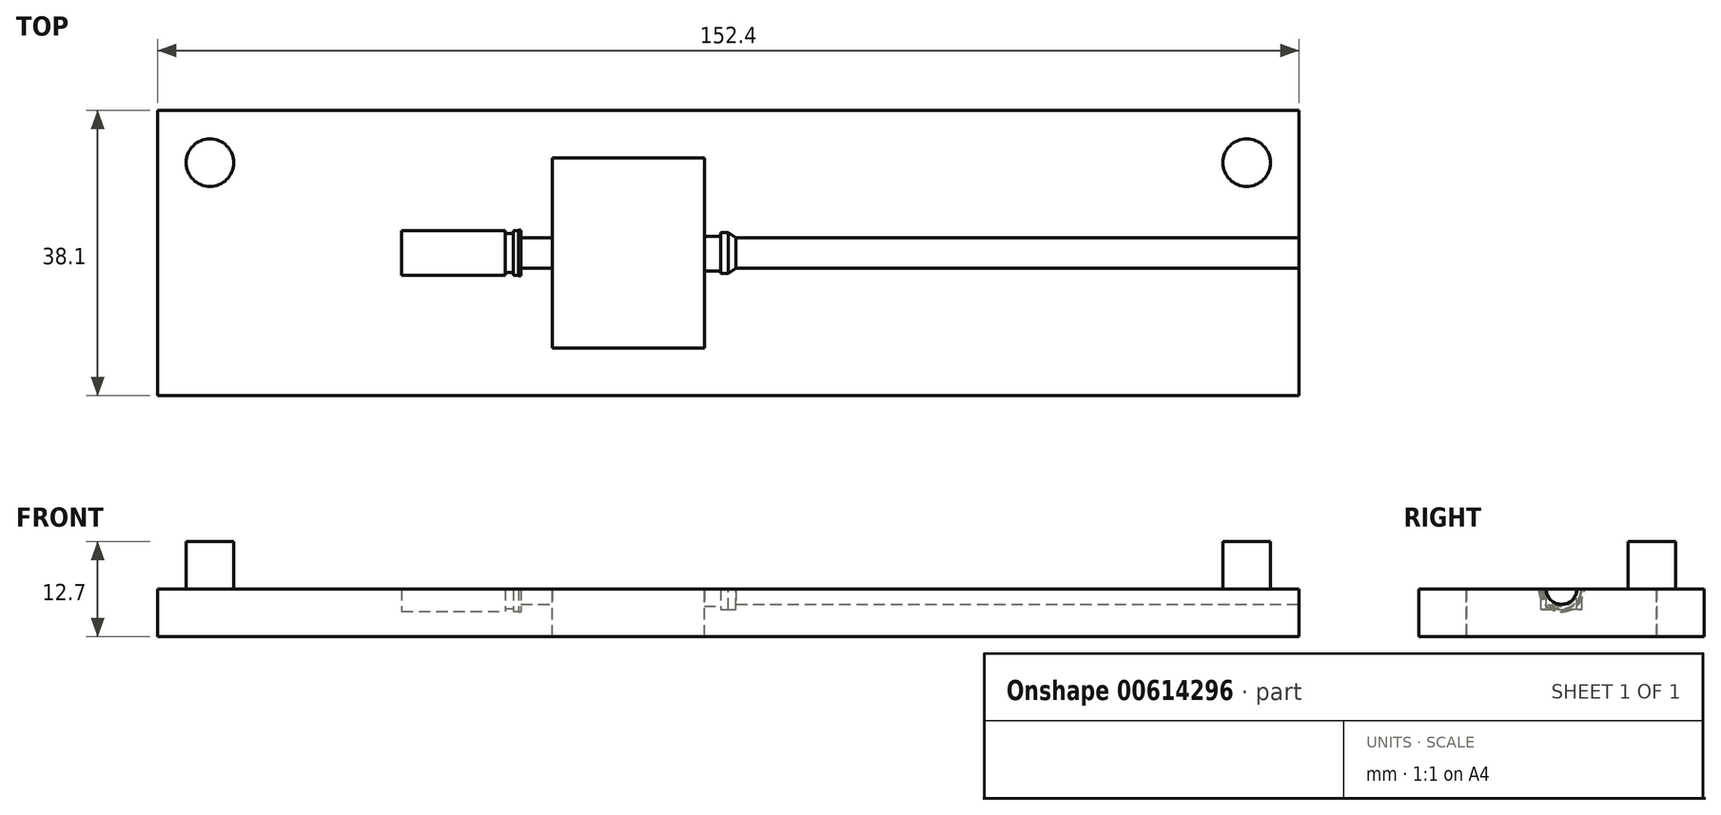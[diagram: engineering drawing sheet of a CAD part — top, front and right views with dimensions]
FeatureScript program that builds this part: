
annotation { "Feature Type Name" : "Feature", "Feature Type Description" : "" }
export const myFeature = defineFeature(function(context is Context, id is Id, definition is map)
    precondition{}
    {
        {
            var Q0;
            Q0=qCreatedBy(makeId("Top.planeOp"),FACE);
            var sketch = newSketch(context, id + "F0", { "sketchPlane" : qUnion([Q0])});
            skLineSegment(sketch, "E0.bottom", {"start": v(-76.2, 19.05) * mm, "end": v(76.2, 19.05) * mm});
            skLineSegment(sketch, "E0.top", {"start": v(-76.2, -19.05) * mm, "end": v(76.2, -19.05) * mm});
            skLineSegment(sketch, "E0.left", {"start": v(-76.2, 19.05) * mm, "end": v(-76.2, -19.05) * mm});
            skLineSegment(sketch, "E0.right", {"start": v(76.2, 19.05) * mm, "end": v(76.2, -19.05) * mm});
            skPoint(sketch, "E0.middle", {"position": v(0, 0) * mm});
            skSolve(sketch);
        }
        {
            var Q0;
            Q0=makeQuery(id+"F0.imprint","IMPRINT",FACE,{"disambiguationData":[TD([[makeQuery(id+"F0.imprint","IMPRINT",EDGE,{"derivedFrom":sQuery(id+"F0.wireOp",EDGE,"E0.bottom")}),-1.0]])]});
            extrude(context, id + "F1", {"entities" : qUnion([Q0]), "depth" : 6.35 * mm, "offsetDistance" : 25.4 * mm});
        }
        {
            var Q0;
            Q0=makeQuery(id+"F1.opExtrude","SWEPT_FACE",FACE,{"disambiguationData":[OSD([sQuery(id+"F0.wireOp",EDGE,"E0.right")])]});
            var sketch = newSketch(context, id + "F2", { "sketchPlane" : qUnion([Q0])});
            skCircle(sketch, "E1", {"center": v(0, 6.35) * mm, "radius": 2.04 * mm});
            skSolve(sketch);
        }
        {
            var Q0;
            Q0=qSketchRegion(id+"F2",true);
            extrude(context, id + "F3", {"entities" : qUnion([Q0]), "operationType" : NewBodyOperationType.ADD, "depth" : -76.2 * mm, "offsetDistance" : 25.4 * mm});
        }
        {
            var Q0;
            Q0=qSketchRegion(id+"F2",true);
            extrude(context, id + "F4", {"entities" : qUnion([Q0]), "operationType" : NewBodyOperationType.REMOVE, "oppositeDirection" : true, "depth" : 76.2 * mm, "offsetDistance" : 25.4 * mm});
        }
        {
            var Q0;
            Q0=makeQuery(id+"F4.boolean.opBoolean","COPY",FACE,{"derivedFrom":makeQuery(id+"F4.opExtrude","CAP_FACE",FACE,{"disambiguationData":[OSD([sQuery(id+"F2.wireOp",EDGE,"E1")])],"isStart":false})});
            var sketch = newSketch(context, id + "F5", { "sketchPlane" : qUnion([Q0])});
            skCircle(sketch, "E2", {"center": v(0, 6.35) * mm, "radius": 2.73 * mm});
            skSolve(sketch);
        }
        {
            var Q0;
            Q0=qSketchRegion(id+"F5",true);
            extrude(context, id + "F6", {"entities" : qUnion([Q0]), "operationType" : NewBodyOperationType.REMOVE, "depth" : -1.02 * mm, "offsetDistance" : 25.4 * mm});
        }
        {
            var Q0;
            Q0=makeQuery(id+"F6.boolean.opBoolean","COPY",FACE,{"derivedFrom":makeQuery(id+"F6.opExtrude","CAP_FACE",FACE,{"disambiguationData":[OSD([sQuery(id+"F5.wireOp",EDGE,"E2")])],"isStart":false})});
            var sketch = newSketch(context, id + "F7", { "sketchPlane" : qUnion([Q0])});
            skCircle(sketch, "E3", {"center": v(-0.1, 6.35) * mm, "radius": 2.31 * mm});
            skSolve(sketch);
        }
        {
            var Q0;
            {var subQ0=sQuery(id+"F7.wireOp",EDGE,"E3");var subQ1=makeQuery(id+"F6.boolean.opBoolean","INTERSECT",EDGE,{"derivedFrom":[makeQuery(id+"F1.opExtrude","CAP_FACE",FACE,{"disambiguationData":[OSD([sQuery(id+"F0.wireOp",EDGE,"E0.bottom"),sQuery(id+"F0.wireOp",EDGE,"E0.top"),sQuery(id+"F0.wireOp",EDGE,"E0.left"),sQuery(id+"F0.wireOp",EDGE,"E0.right")])],"isStart":false}),makeQuery(id+"F6.opExtrude","CAP_FACE",FACE,{"disambiguationData":[OSD([sQuery(id+"F5.wireOp",EDGE,"E2")])],"isStart":false})]});var subQ2=makeQuery(id+"F7.imprint","INTERSECT",VERTEX,{"disambiguationData":[OD(0.0)],"derivedFrom":[subQ1,subQ0]});Q0=makeQuery(id+"F7.imprint","IMPRINT",FACE,{"disambiguationData":[TD([[makeQuery(id+"F7.imprint","IMPRINT",EDGE,{"disambiguationData":[TD([[subQ2,1.0]])],"derivedFrom":subQ0}),1.0]])]});}
            extrude(context, id + "F8", {"entities" : qUnion([Q0]), "operationType" : NewBodyOperationType.REMOVE, "depth" : -7.62 * mm, "offsetDistance" : 25.4 * mm});
        }
        {
            var Q0;
            Q0=makeQuery(id+"F8.boolean.opBoolean","COPY",FACE,{"derivedFrom":makeQuery(id+"F8.opExtrude","CAP_FACE",FACE,{"disambiguationData":[OSD([sQuery(id+"F0.wireOp",EDGE,"E0.bottom"),sQuery(id+"F0.wireOp",EDGE,"E0.top"),sQuery(id+"F0.wireOp",EDGE,"E0.left"),sQuery(id+"F0.wireOp",EDGE,"E0.right"),sQuery(id+"F5.wireOp",EDGE,"E2"),sQuery(id+"F7.wireOp",EDGE,"E3")])],"isStart":false})});
            var sketch = newSketch(context, id + "F9", { "sketchPlane" : qUnion([Q0])});
            skCircle(sketch, "E4", {"center": v(-0.1, 6.35) * mm, "radius": 3.6 * mm});
            skSolve(sketch);
        }
        {
            var Q0;
            Q0=qSketchRegion(id+"F9",true);
            extrude(context, id + "F10", {"entities" : qUnion([Q0]), "operationType" : NewBodyOperationType.REMOVE, "oppositeDirection" : true, "depth" : -1.9 * mm, "offsetDistance" : 25.4 * mm});
        }
        {
            var Q0;
            Q0=makeQuery(id+"F10.boolean.opBoolean","MERGE",FACE,{"derivedFrom":[makeQuery(id+"F8.boolean.opBoolean","COPY",FACE,{"derivedFrom":makeQuery(id+"F8.opExtrude","CAP_FACE",FACE,{"disambiguationData":[OSD([sQuery(id+"F0.wireOp",EDGE,"E0.bottom"),sQuery(id+"F0.wireOp",EDGE,"E0.top"),sQuery(id+"F0.wireOp",EDGE,"E0.left"),sQuery(id+"F0.wireOp",EDGE,"E0.right"),sQuery(id+"F5.wireOp",EDGE,"E2"),sQuery(id+"F7.wireOp",EDGE,"E3")])],"isStart":false})}),makeQuery(id+"F10.opExtrude","CAP_FACE",FACE,{"disambiguationData":[OSD([sQuery(id+"F9.wireOp",EDGE,"E4")])],"isStart":true})]});
            var sketch = newSketch(context, id + "F11", { "sketchPlane" : qUnion([Q0])});
            skCircle(sketch, "E5", {"center": v(0, 6.35) * mm, "radius": 4.76 * mm});
            skSolve(sketch);
        }
        {
            var Q0;
            Q0=makeQuery(id+"F11.imprint","IMPRINT",FACE,{"disambiguationData":[TD([[makeQuery(id+"F11.imprint","IMPRINT",EDGE,{"derivedFrom":sQuery(id+"F11.wireOp",EDGE,"E5")}),1.0]])]});
            extrude(context, id + "F12", {"entities" : qUnion([Q0]), "operationType" : NewBodyOperationType.REMOVE, "oppositeDirection" : true, "depth" : -0.64 * mm, "offsetDistance" : 25.4 * mm});
        }
        {
            var Q0;
            {var subQ0=sQuery(id+"F9.wireOp",EDGE,"E4");var subQ1=sQuery(id+"F0.wireOp",EDGE,"E0.right");var subQ2=sQuery(id+"F0.wireOp",EDGE,"E0.left");var subQ3=sQuery(id+"F0.wireOp",EDGE,"E0.top");var subQ4=sQuery(id+"F0.wireOp",EDGE,"E0.bottom");Q0=makeQuery(id+"F12.boolean.opBoolean","MERGE",FACE,{"derivedFrom":[makeQuery(id+"F10.boolean.opBoolean","MERGE",FACE,{"derivedFrom":[makeQuery(id+"F8.boolean.opBoolean","COPY",FACE,{"derivedFrom":makeQuery(id+"F8.opExtrude","CAP_FACE",FACE,{"disambiguationData":[OSD([subQ4,subQ3,subQ2,subQ1,sQuery(id+"F5.wireOp",EDGE,"E2"),sQuery(id+"F7.wireOp",EDGE,"E3")])],"isStart":false})}),makeQuery(id+"F10.opExtrude","CAP_FACE",FACE,{"disambiguationData":[OSD([subQ0])],"isStart":true})]}),makeQuery(id+"F12.opExtrude","CAP_FACE",FACE,{"disambiguationData":[OSD([subQ4,subQ3,subQ2,subQ1,subQ0,sQuery(id+"F11.wireOp",EDGE,"E5")])],"isStart":true})]});}
            var sketch = newSketch(context, id + "F13", { "sketchPlane" : qUnion([Q0])});
            skCircle(sketch, "E6", {"center": v(0, 6.35) * mm, "radius": 1.52 * mm});
            skSolve(sketch);
        }
        {
            var Q0;
            Q0=qSketchRegion(id+"F13",true);
            extrude(context, id + "F14", {"entities" : qUnion([Q0]), "operationType" : NewBodyOperationType.REMOVE, "oppositeDirection" : true, "depth" : 1 * mm, "offsetDistance" : 25.4 * mm});
        }
        {
            var Q0;
            Q0=makeQuery(id+"F14.boolean.opBoolean","COPY",FACE,{"derivedFrom":makeQuery(id+"F14.opExtrude","CAP_FACE",FACE,{"disambiguationData":[OSD([sQuery(id+"F13.wireOp",EDGE,"E6")])],"isStart":false})});
            var sketch = newSketch(context, id + "F15", { "sketchPlane" : qUnion([Q0])});
            skLineSegment(sketch, "E7.bottom", {"start": v(-12.7, -12.7) * mm, "end": v(12.7, -12.7) * mm});
            skLineSegment(sketch, "E7.top", {"start": v(-12.7, 25.4) * mm, "end": v(12.7, 25.4) * mm});
            skLineSegment(sketch, "E7.left", {"start": v(-12.7, -12.7) * mm, "end": v(-12.7, 25.4) * mm});
            skLineSegment(sketch, "E7.right", {"start": v(12.7, -12.7) * mm, "end": v(12.7, 25.4) * mm});
            skPoint(sketch, "E7.middle", {"position": v(0, 6.35) * mm});
            skSolve(sketch);
        }
        {
            var Q0;
            Q0=qSketchRegion(id+"F15",true);
            extrude(context, id + "F16", {"entities" : qUnion([Q0]), "operationType" : NewBodyOperationType.REMOVE, "oppositeDirection" : true, "depth" : 7.62 * mm, "offsetDistance" : 25.4 * mm});
        }
        {
            var Q0;
            Q0=makeQuery(id+"F16.boolean.opBoolean","COPY",FACE,{"derivedFrom":makeQuery(id+"F16.opExtrude","CAP_FACE",FACE,{"disambiguationData":[OSD([sQuery(id+"F15.wireOp",EDGE,"E7.bottom"),sQuery(id+"F15.wireOp",EDGE,"E7.top"),sQuery(id+"F15.wireOp",EDGE,"E7.left"),sQuery(id+"F15.wireOp",EDGE,"E7.right")])],"isStart":false})});
            var sketch = newSketch(context, id + "F17", { "sketchPlane" : qUnion([Q0])});
            skCircle(sketch, "E8", {"center": v(0, 6.35) * mm, "radius": 1.52 * mm});
            skSolve(sketch);
        }
        {
            var Q0;
            {var subQ0=sQuery(id+"F17.wireOp",EDGE,"E8");var subQ1=makeQuery(id+"F16.boolean.opBoolean","INTERSECT",EDGE,{"derivedFrom":[makeQuery(id+"F1.opExtrude","CAP_FACE",FACE,{"disambiguationData":[OSD([sQuery(id+"F0.wireOp",EDGE,"E0.bottom"),sQuery(id+"F0.wireOp",EDGE,"E0.top"),sQuery(id+"F0.wireOp",EDGE,"E0.left"),sQuery(id+"F0.wireOp",EDGE,"E0.right")])],"isStart":false}),makeQuery(id+"F16.opExtrude","CAP_FACE",FACE,{"disambiguationData":[OSD([sQuery(id+"F15.wireOp",EDGE,"E7.bottom"),sQuery(id+"F15.wireOp",EDGE,"E7.top"),sQuery(id+"F15.wireOp",EDGE,"E7.left"),sQuery(id+"F15.wireOp",EDGE,"E7.right")])],"isStart":false})]});var subQ2=makeQuery(id+"F17.imprint","INTERSECT",VERTEX,{"disambiguationData":[OD(0.0)],"derivedFrom":[subQ1,subQ0]});Q0=makeQuery(id+"F17.imprint","IMPRINT",FACE,{"disambiguationData":[TD([[makeQuery(id+"F17.imprint","IMPRINT",EDGE,{"disambiguationData":[TD([[subQ2,1.0]])],"derivedFrom":subQ0}),1.0]])]});}
            var Q1;
            {var subQ0=sQuery(id+"F17.wireOp",EDGE,"E8");var subQ1=makeQuery(id+"F16.boolean.opBoolean","INTERSECT",EDGE,{"derivedFrom":[makeQuery(id+"F1.opExtrude","CAP_FACE",FACE,{"disambiguationData":[OSD([sQuery(id+"F0.wireOp",EDGE,"E0.bottom"),sQuery(id+"F0.wireOp",EDGE,"E0.top"),sQuery(id+"F0.wireOp",EDGE,"E0.left"),sQuery(id+"F0.wireOp",EDGE,"E0.right")])],"isStart":false}),makeQuery(id+"F16.opExtrude","CAP_FACE",FACE,{"disambiguationData":[OSD([sQuery(id+"F15.wireOp",EDGE,"E7.bottom"),sQuery(id+"F15.wireOp",EDGE,"E7.top"),sQuery(id+"F15.wireOp",EDGE,"E7.left"),sQuery(id+"F15.wireOp",EDGE,"E7.right")])],"isStart":false})]});var subQ2=makeQuery(id+"F17.imprint","INTERSECT",VERTEX,{"disambiguationData":[OD(0.0)],"derivedFrom":[subQ1,subQ0]});Q1=makeQuery(id+"F17.imprint","IMPRINT",FACE,{"disambiguationData":[TD([[makeQuery(id+"F17.imprint","IMPRINT",EDGE,{"disambiguationData":[TD([[subQ2,-1.0]])],"derivedFrom":subQ0}),1.0]])]});}
            extrude(context, id + "F18", {"entities" : qUnion([Q0, Q1]), "operationType" : NewBodyOperationType.REMOVE, "oppositeDirection" : true, "depth" : 1.27 * mm, "offsetDistance" : 25.4 * mm});
        }
        {
            var Q0;
            Q0=makeQuery(id+"F18.boolean.opBoolean","COPY",FACE,{"derivedFrom":makeQuery(id+"F18.opExtrude","CAP_FACE",FACE,{"disambiguationData":[OSD([sQuery(id+"F17.wireOp",EDGE,"E8")])],"isStart":false})});
            var sketch = newSketch(context, id + "F19", { "sketchPlane" : qUnion([Q0])});
            skCircle(sketch, "E9", {"center": v(0, 6.35) * mm, "radius": 3.21 * mm});
            skSolve(sketch);
        }
        {
            var Q0;
            Q0=makeQuery(id+"F19.imprint","IMPRINT",FACE,{"disambiguationData":[TD([[makeQuery(id+"F19.imprint","IMPRINT",EDGE,{"derivedFrom":sQuery(id+"F19.wireOp",EDGE,"E9")}),1.0]])]});
            extrude(context, id + "F20", {"entities" : qUnion([Q0]), "operationType" : NewBodyOperationType.REMOVE, "depth" : 0.5 * mm, "offsetDistance" : 25.4 * mm});
        }
        {
            var Q0;
            {var subQ0=sQuery(id+"F17.wireOp",EDGE,"E8");Q0=makeQuery(id+"F20.boolean.opBoolean","MERGE",FACE,{"derivedFrom":[makeQuery(id+"F18.boolean.opBoolean","COPY",FACE,{"derivedFrom":makeQuery(id+"F18.opExtrude","CAP_FACE",FACE,{"disambiguationData":[OSD([subQ0])],"isStart":false})}),makeQuery(id+"F20.opExtrude","CAP_FACE",FACE,{"disambiguationData":[OSD([sQuery(id+"F0.wireOp",EDGE,"E0.bottom"),sQuery(id+"F0.wireOp",EDGE,"E0.top"),sQuery(id+"F0.wireOp",EDGE,"E0.left"),sQuery(id+"F0.wireOp",EDGE,"E0.right"),subQ0,sQuery(id+"F19.wireOp",EDGE,"E9")])],"isStart":true})]});}
            var sketch = newSketch(context, id + "F21", { "sketchPlane" : qUnion([Q0])});
            skCircle(sketch, "E10", {"center": v(0, 6.35) * mm, "radius": 2.93 * mm});
            skSolve(sketch);
        }
        {
            var Q0;
            {var subQ0=sQuery(id+"F21.wireOp",EDGE,"E10");var subQ1=makeQuery(id+"F18.boolean.opBoolean","INTERSECT",EDGE,{"derivedFrom":[makeQuery(id+"F1.opExtrude","CAP_FACE",FACE,{"disambiguationData":[OSD([sQuery(id+"F0.wireOp",EDGE,"E0.bottom"),sQuery(id+"F0.wireOp",EDGE,"E0.top"),sQuery(id+"F0.wireOp",EDGE,"E0.left"),sQuery(id+"F0.wireOp",EDGE,"E0.right")])],"isStart":false}),makeQuery(id+"F18.opExtrude","CAP_FACE",FACE,{"disambiguationData":[OSD([sQuery(id+"F17.wireOp",EDGE,"E8")])],"isStart":false})]});var subQ2=makeQuery(id+"F21.imprint","INTERSECT",VERTEX,{"disambiguationData":[OD(0.0)],"derivedFrom":[subQ1,subQ0]});Q0=makeQuery(id+"F21.imprint","IMPRINT",FACE,{"disambiguationData":[TD([[makeQuery(id+"F21.imprint","IMPRINT",EDGE,{"disambiguationData":[TD([[subQ2,1.0]])],"derivedFrom":subQ0}),1.0]])]});}
            var Q1;
            {var subQ0=sQuery(id+"F21.wireOp",EDGE,"E10");var subQ1=makeQuery(id+"F18.boolean.opBoolean","INTERSECT",EDGE,{"derivedFrom":[makeQuery(id+"F1.opExtrude","CAP_FACE",FACE,{"disambiguationData":[OSD([sQuery(id+"F0.wireOp",EDGE,"E0.bottom"),sQuery(id+"F0.wireOp",EDGE,"E0.top"),sQuery(id+"F0.wireOp",EDGE,"E0.left"),sQuery(id+"F0.wireOp",EDGE,"E0.right")])],"isStart":false}),makeQuery(id+"F18.opExtrude","CAP_FACE",FACE,{"disambiguationData":[OSD([sQuery(id+"F17.wireOp",EDGE,"E8")])],"isStart":false})]});var subQ2=makeQuery(id+"F21.imprint","INTERSECT",VERTEX,{"disambiguationData":[OD(0.0)],"derivedFrom":[subQ1,subQ0]});Q1=makeQuery(id+"F21.imprint","IMPRINT",FACE,{"disambiguationData":[TD([[makeQuery(id+"F21.imprint","IMPRINT",EDGE,{"disambiguationData":[TD([[subQ2,-1.0]])],"derivedFrom":subQ0}),1.0]])]});}
            extrude(context, id + "F22", {"entities" : qUnion([Q0, Q1]), "operationType" : NewBodyOperationType.REMOVE, "oppositeDirection" : true, "depth" : 0.76 * mm, "offsetDistance" : 25.4 * mm});
        }
        {
            var Q0;
            Q0=makeQuery(id+"F22.boolean.opBoolean","COPY",FACE,{"derivedFrom":makeQuery(id+"F22.opExtrude","CAP_FACE",FACE,{"disambiguationData":[OSD([sQuery(id+"F21.wireOp",EDGE,"E10")])],"isStart":false})});
            var sketch = newSketch(context, id + "F23", { "sketchPlane" : qUnion([Q0])});
            skCircle(sketch, "E11", {"center": v(0, 6.35) * mm, "radius": 2.03 * mm});
            skSolve(sketch);
        }
        {
            var Q0;
            Q0=qSketchRegion(id+"F23",true);
            extrude(context, id + "F24", {"entities" : qUnion([Q0]), "operationType" : NewBodyOperationType.REMOVE, "oppositeDirection" : true, "depth" : 8.38 * mm, "offsetDistance" : 25.4 * mm});
        }
        {
            var Q0;
            Q0=makeQuery(id+"F24.boolean.opBoolean","COPY",FACE,{"derivedFrom":makeQuery(id+"F24.opExtrude","CAP_FACE",FACE,{"disambiguationData":[OSD([sQuery(id+"F23.wireOp",EDGE,"E11")])],"isStart":false})});
            var sketch = newSketch(context, id + "F25", { "sketchPlane" : qUnion([Q0])});
            skCircle(sketch, "E12", {"center": v(0, 6.35) * mm, "radius": 3.05 * mm});
            skSolve(sketch);
        }
        {
            var Q0;
            Q0=qSketchRegion(id+"F25",true);
            extrude(context, id + "F26", {"entities" : qUnion([Q0]), "operationType" : NewBodyOperationType.REMOVE, "oppositeDirection" : true, "depth" : 0.36 * mm, "offsetDistance" : 25.4 * mm});
        }
        {
            var Q0;
            Q0=makeQuery(id+"F26.boolean.opBoolean","COPY",FACE,{"derivedFrom":makeQuery(id+"F26.opExtrude","CAP_FACE",FACE,{"disambiguationData":[OSD([sQuery(id+"F25.wireOp",EDGE,"E12")])],"isStart":false})});
            var sketch = newSketch(context, id + "F27", { "sketchPlane" : qUnion([Q0])});
            skCircle(sketch, "E13", {"center": v(0, 6.35) * mm, "radius": 2.97 * mm});
            skSolve(sketch);
        }
        {
            var Q0;
            Q0=qSketchRegion(id+"F27",true);
            extrude(context, id + "F28", {"entities" : qUnion([Q0]), "operationType" : NewBodyOperationType.REMOVE, "oppositeDirection" : true, "depth" : 0.66 * mm, "offsetDistance" : 25.4 * mm});
        }
        {
            var Q0;
            Q0=makeQuery(id+"F28.boolean.opBoolean","COPY",FACE,{"derivedFrom":makeQuery(id+"F28.opExtrude","CAP_FACE",FACE,{"disambiguationData":[OSD([sQuery(id+"F27.wireOp",EDGE,"E13")])],"isStart":false})});
            var sketch = newSketch(context, id + "F29", { "sketchPlane" : qUnion([Q0])});
            skCircle(sketch, "E14", {"center": v(0, 6.35) * mm, "radius": 2.62 * mm});
            skSolve(sketch);
        }
        {
            var Q0;
            Q0=qSketchRegion(id+"F29",true);
            extrude(context, id + "F30", {"entities" : qUnion([Q0]), "operationType" : NewBodyOperationType.REMOVE, "oppositeDirection" : true, "depth" : 1.12 * mm, "offsetDistance" : 25.4 * mm});
        }
        {
            var Q0;
            Q0=makeQuery(id+"F30.boolean.opBoolean","COPY",FACE,{"derivedFrom":makeQuery(id+"F30.opExtrude","CAP_FACE",FACE,{"disambiguationData":[OSD([sQuery(id+"F29.wireOp",EDGE,"E14")])],"isStart":false})});
            var sketch = newSketch(context, id + "F31", { "sketchPlane" : qUnion([Q0])});
            skCircle(sketch, "E15", {"center": v(0, 6.35) * mm, "radius": 2.98 * mm});
            skSolve(sketch);
        }
        {
            var Q0;
            Q0=qSketchRegion(id+"F31",true);
            extrude(context, id + "F32", {"entities" : qUnion([Q0]), "operationType" : NewBodyOperationType.REMOVE, "oppositeDirection" : true, "depth" : 13.8 * mm, "offsetDistance" : 25.4 * mm});
        }
        {
            var Q0;
            Q0=makeQuery(id+"F1.opExtrude","CAP_FACE",FACE,{"disambiguationData":[OSD([sQuery(id+"F0.wireOp",EDGE,"E0.bottom"),sQuery(id+"F0.wireOp",EDGE,"E0.top"),sQuery(id+"F0.wireOp",EDGE,"E0.left"),sQuery(id+"F0.wireOp",EDGE,"E0.right")])],"isStart":false});
            var sketch = newSketch(context, id + "F33", { "sketchPlane" : qUnion([Q0])});
            skCircle(sketch, "E16", {"center": v(-69.22, 12.06) * mm, "radius": 3.18 * mm});
            skCircle(sketch, "E17", {"center": v(69.22, 12.06) * mm, "radius": 3.18 * mm});
            skSolve(sketch);
        }
        {
            var Q0;
            Q0=qSketchRegion(id+"F33",true);
            extrude(context, id + "F34", {"entities" : qUnion([Q0]), "operationType" : NewBodyOperationType.ADD, "oppositeDirection" : true, "depth" : -6.35 * mm, "offsetDistance" : 25.4 * mm});
        }
        {
            var Q0;
            Q0=makeQuery(id+"F1.opExtrude","CAP_FACE",FACE,{"disambiguationData":[OSD([sQuery(id+"F0.wireOp",EDGE,"E0.bottom"),sQuery(id+"F0.wireOp",EDGE,"E0.top"),sQuery(id+"F0.wireOp",EDGE,"E0.left"),sQuery(id+"F0.wireOp",EDGE,"E0.right")])],"isStart":false});
            var sketch = newSketch(context, id + "F35", { "sketchPlane" : qUnion([Q0])});
            skLineSegment(sketch, "E18", {"start": v(0, 2.73) * mm, "end": v(1.02, 2.04) * mm});
            skLineSegment(sketch, "E19", {"start": v(1.02, 2.04) * mm, "end": v(1.02, -2.04) * mm});
            skLineSegment(sketch, "E20", {"start": v(1.02, -2.04) * mm, "end": v(0, -2.73) * mm});
            skLineSegment(sketch, "E21", {"start": v(0, -2.73) * mm, "end": v(0, 2.73) * mm});
            skSolve(sketch);
        }
        {
            var Q0;
            Q0=qSketchRegion(id+"F35",true);
            extrude(context, id + "F36", {"entities" : qUnion([Q0]), "operationType" : NewBodyOperationType.REMOVE, "oppositeDirection" : true, "depth" : 2.73 * mm, "offsetDistance" : 25.4 * mm});
        }
        {
            var Q0;
            Q0=makeQuery(id+"F1.opExtrude","CAP_FACE",FACE,{"disambiguationData":[OSD([sQuery(id+"F0.wireOp",EDGE,"E0.bottom"),sQuery(id+"F0.wireOp",EDGE,"E0.top"),sQuery(id+"F0.wireOp",EDGE,"E0.left"),sQuery(id+"F0.wireOp",EDGE,"E0.right")])],"isStart":false});
            var sketch = newSketch(context, id + "F37", { "sketchPlane" : qUnion([Q0])});
            skLineSegment(sketch, "E22.bottom", {"start": v(-23.52, 12.7) * mm, "end": v(-3.2, 12.7) * mm});
            skLineSegment(sketch, "E22.top", {"start": v(-23.52, -12.7) * mm, "end": v(-3.2, -12.7) * mm});
            skLineSegment(sketch, "E22.left", {"start": v(-23.52, 12.7) * mm, "end": v(-23.52, -12.7) * mm});
            skLineSegment(sketch, "E22.right", {"start": v(-3.2, 12.7) * mm, "end": v(-3.2, -12.7) * mm});
            skPoint(sketch, "E22.middle", {"position": v(-13.36, 0) * mm});
            skSolve(sketch);
        }
        {
            var Q0;
            Q0 = qSketchRegion(id + "F37", true);
            extrude(context, id + "F38", {"entities" : qUnion([Q0]), "operationType" : NewBodyOperationType.REMOVE, "oppositeDirection" : true, "depth" : 25.4 * mm, "offsetDistance" : 25.4 * mm});
        }
    });
